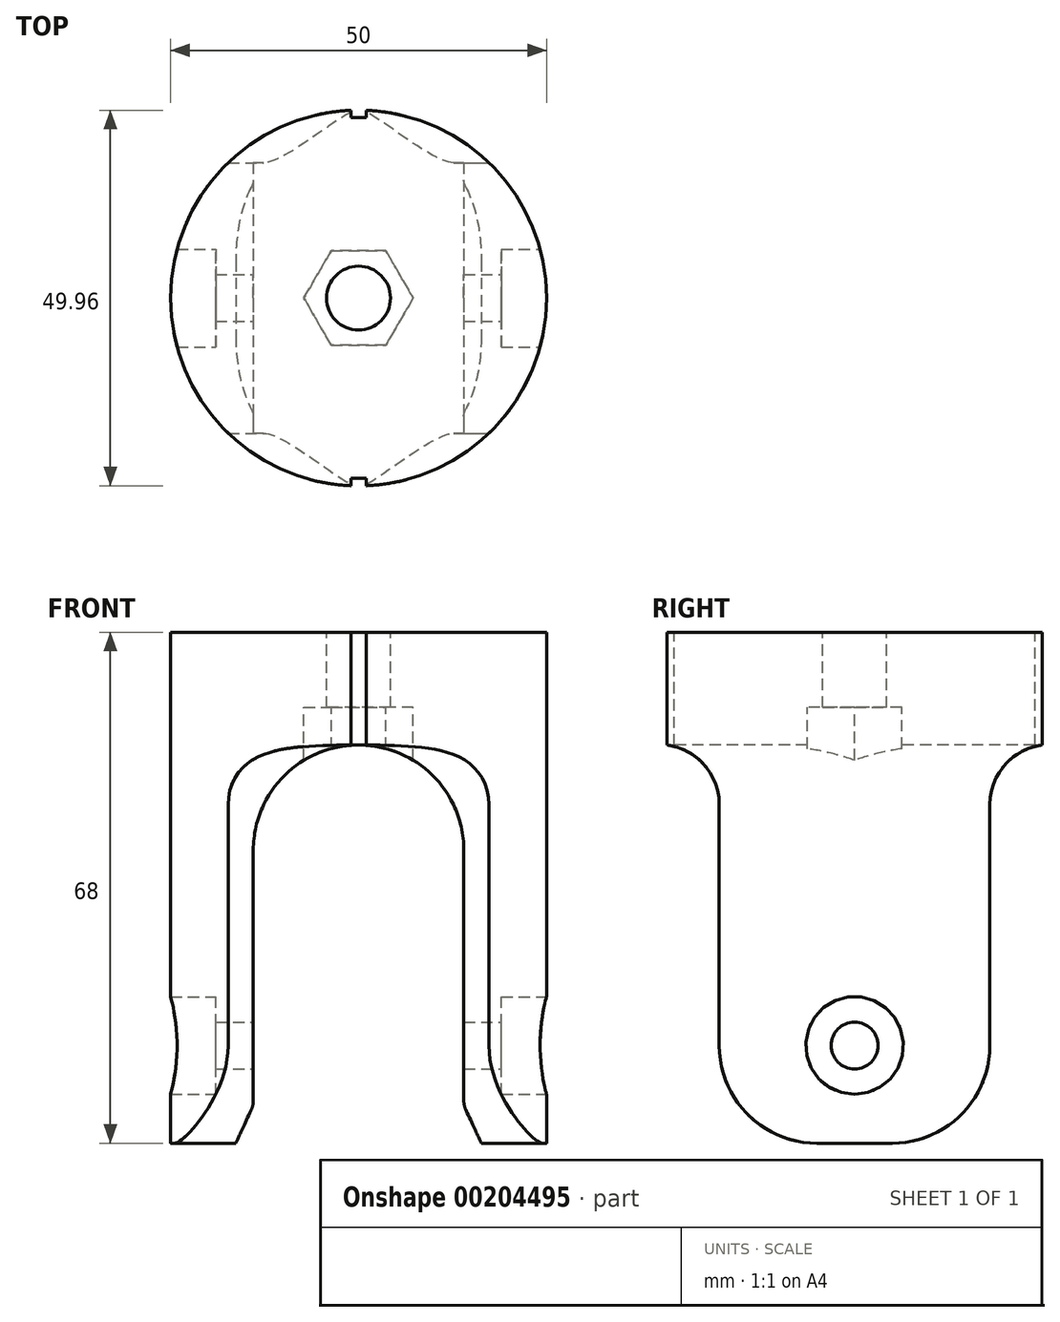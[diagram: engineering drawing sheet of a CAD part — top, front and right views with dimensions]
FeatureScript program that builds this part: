
annotation { "Feature Type Name" : "Feature", "Feature Type Description" : "" }
export const myFeature = defineFeature(function(context is Context, id is Id, definition is map)
    precondition{}
    {
        {
            var Q0;
            Q0=qCreatedBy(makeId("Top.planeOp"),FACE);
            var sketch = newSketch(context, id + "F0", { "sketchPlane" : qUnion([Q0])});
            skCircle(sketch, "E0", {"center": v(0, 0) * mm, "radius": 25 * mm});
            skSolve(sketch);
        }
        {
            var Q0;
            Q0 = qSketchRegion(id + "F0", true);
            extrude(context, id + "F1", {"entities" : qUnion([Q0]), "oppositeDirection" : true, "depth" : 68 * mm});
        }
        {
            var Q0;
            Q0=qCreatedBy(makeId("Right.planeOp"),FACE);
            var sketch = newSketch(context, id + "F2", { "sketchPlane" : qUnion([Q0])});
            skCircle(sketch, "E1", {"center": v(0, -55) * mm, "radius": 40 * mm, "construction": true});
            skLineSegment(sketch, "E2", {"start": v(-28, -15) * mm, "end": v(-25, -15) * mm});
            skLineSegment(sketch, "E3", {"start": v(-18, -22.94) * mm, "end": v(-18, -55) * mm});
            skLineSegment(sketch, "E4", {"start": v(-28, -15) * mm, "end": v(-28, -73) * mm});
            skLineSegment(sketch, "E5", {"start": v(-28, -73) * mm, "end": v(0, -73) * mm});
            skLineSegment(sketch, "E6", {"start": v(0, -68) * mm, "end": v(-5, -68) * mm});
            skArc(sketch, "E7", {"start": v(-18, -55) * mm, "mid": v(-14.2, -64.2) * mm, "end": v(-5, -68) * mm});
            skLineSegment(sketch, "E8", {"start": v(0, 0) * mm, "end": v(0, -95) * mm, "construction": true});
            skArc(sketch, "E9", {"start": v(-18, -22.94) * mm, "mid": v(-20, -17.65) * mm, "end": v(-25, -15) * mm});
            skLineSegment(sketch, "E10.MirrorCS", {"start": v(28, -15) * mm, "end": v(25, -15) * mm});
            skArc(sketch, "E11.MirrorCS", {"start": v(18, -22.94) * mm, "mid": v(20, -17.65) * mm, "end": v(25, -15) * mm});
            skArc(sketch, "E12.MirrorCS", {"start": v(18, -55) * mm, "mid": v(14.2, -64.2) * mm, "end": v(5, -68) * mm});
            skLineSegment(sketch, "E13.MirrorCS", {"start": v(0, -68) * mm, "end": v(5, -68) * mm});
            skLineSegment(sketch, "E14.MirrorCS", {"start": v(18, -22.94) * mm, "end": v(18, -55) * mm});
            skLineSegment(sketch, "E15.MirrorCS", {"start": v(28, -73) * mm, "end": v(0, -73) * mm});
            skLineSegment(sketch, "E16.MirrorCS", {"start": v(28, -15) * mm, "end": v(28, -73) * mm});
            skSolve(sketch);
        }
        {
            var Q0;
            Q0 = qSketchRegion(id + "F2", true);
            extrude(context, id + "F3", {"entities" : qUnion([Q0]), "operationType" : NewBodyOperationType.REMOVE, "endBound" : BoundingType.THROUGH_ALL, "oppositeDirection" : true, "depth" : 25 * mm, "hasSecondDirection" : true, "secondDirectionBound" : SecondDirectionBoundingType.THROUGH_ALL, "secondDirectionOppositeDirection" : false, "secondDirectionDepth" : 25 * mm});
        }
        {
            var Q0;
            Q0=qCreatedBy(makeId("Front.planeOp"),FACE);
            var sketch = newSketch(context, id + "F4", { "sketchPlane" : qUnion([Q0])});
            skArc(sketch, "E17", {"start": v(14, -29) * mm, "mid": v(0, -15) * mm, "end": v(-14, -29) * mm});
            skLineSegment(sketch, "E18", {"start": v(-14, -29) * mm, "end": v(-14, -62.33) * mm});
            skLineSegment(sketch, "E19", {"start": v(14, -29) * mm, "end": v(14, -62.33) * mm});
            skLineSegment(sketch, "E20", {"start": v(16.33, -68) * mm, "end": v(-16.33, -68) * mm});
            skLineSegment(sketch, "E21", {"start": v(-14.28, -63.6) * mm, "end": v(-16.33, -68) * mm});
            skLineSegment(sketch, "E22", {"start": v(14.28, -63.6) * mm, "end": v(16.33, -68) * mm});
            skLineSegment(sketch, "E23", {"start": v(-14, -63) * mm, "end": v(14, -63) * mm, "construction": true});
            skPoint(sketch, "E24.visualSharp", {"position": v(-14, -63) * mm});
            skArc(sketch, "E24.filletArc", {"start": v(-14.28, -63.6) * mm, "mid": v(-14.07, -62.98) * mm, "end": v(-14, -62.33) * mm});
            skPoint(sketch, "E25.visualSharp", {"position": v(14, -63) * mm});
            skArc(sketch, "E25.filletArc", {"start": v(14, -62.33) * mm, "mid": v(14.07, -62.98) * mm, "end": v(14.28, -63.6) * mm});
            skSolve(sketch);
        }
        {
            var Q0;
            Q0 = qSketchRegion(id + "F4", true);
            extrude(context, id + "F5", {"entities" : qUnion([Q0]), "operationType" : NewBodyOperationType.REMOVE, "endBound" : BoundingType.THROUGH_ALL, "oppositeDirection" : true, "depth" : 25 * mm, "hasSecondDirection" : true, "secondDirectionBound" : SecondDirectionBoundingType.THROUGH_ALL, "secondDirectionOppositeDirection" : false, "secondDirectionDepth" : 25 * mm});
        }
        {
            var Q0;
            Q0=qCreatedBy(makeId("Front.planeOp"),FACE);
            var sketch = newSketch(context, id + "F6", { "sketchPlane" : qUnion([Q0])});
            skLineSegment(sketch, "E26", {"start": v(-30.91, -55) * mm, "end": v(31.05, -55) * mm, "construction": true});
            skLineSegment(sketch, "E27", {"start": v(-26, -48.5) * mm, "end": v(-19, -48.5) * mm});
            skLineSegment(sketch, "E28", {"start": v(-19, -48.5) * mm, "end": v(-19, -51.88) * mm});
            skLineSegment(sketch, "E29", {"start": v(-19, -51.88) * mm, "end": v(0, -51.88) * mm});
            skLineSegment(sketch, "E30", {"start": v(-26, -48.5) * mm, "end": v(-26, -55) * mm});
            skLineSegment(sketch, "E31", {"start": v(-26, -55) * mm, "end": v(0, -55) * mm});
            skLineSegment(sketch, "E32.MirrorCS", {"start": v(26, -48.5) * mm, "end": v(19, -48.5) * mm});
            skLineSegment(sketch, "E33.MirrorCS", {"start": v(19, -48.5) * mm, "end": v(19, -51.88) * mm});
            skLineSegment(sketch, "E34.MirrorCS", {"start": v(19, -51.88) * mm, "end": v(0, -51.88) * mm});
            skLineSegment(sketch, "E35.MirrorCS", {"start": v(26, -48.5) * mm, "end": v(26, -55) * mm});
            skLineSegment(sketch, "E36.MirrorCS", {"start": v(26, -55) * mm, "end": v(0, -55) * mm});
            skSolve(sketch);
        }
        {
            var Q0;
            Q0 = qSketchRegion(id + "F6", true);
            var Q1;
            Q1=sQuery(id+"F6.wireOp",EDGE,"E26");
            revolve(context, id + "F7", {"operationType" : NewBodyOperationType.REMOVE, "entities" : qUnion([Q0]), "axis" : qUnion([Q1]), "revolveType" : RevolveType.FULL, "oppositeDirection" : true});
        }
        {
            var Q0;
            Q0=makeQuery(id+"F1.opExtrude","CAP_FACE",FACE,{"disambiguationData":[OSD([sQuery(id+"F0.wireOp",EDGE,"E0")])],"isStart":true});
            var sketch = newSketch(context, id + "F8", { "sketchPlane" : qUnion([Q0])});
            skCircle(sketch, "E37", {"center": v(0, 0) * mm, "radius": 4.25 * mm});
            skSolve(sketch);
        }
        {
            var Q0;
            Q0 = qSketchRegion(id + "F8", true);
            extrude(context, id + "F9", {"entities" : qUnion([Q0]), "operationType" : NewBodyOperationType.REMOVE, "oppositeDirection" : true, "depth" : 25 * mm});
        }
        {
            var Q0;
            Q0=qCreatedBy(makeId("Top.planeOp"),FACE);
            cPlane(context, id + "F10", {"entities" : qUnion([Q0]), "cplaneType" : CPlaneType.OFFSET, "offset" : 10 * mm, "oppositeDirection" : true, "width" : 150 * mm, "height" : 150 * mm});
        }
        {
            var Q0;
            Q0=qCreatedBy(id+"F10.planeOp",FACE);
            var sketch = newSketch(context, id + "F11", { "sketchPlane" : qUnion([Q0])});
            skCircle(sketch, "E38.cCircle", {"center": v(0, 0) * mm, "radius": 6.3 * mm, "construction": true});
            skLineSegment(sketch, "E38.0", {"start": v(7.27, 0) * mm, "end": v(3.64, -6.3) * mm});
            skLineSegment(sketch, "E38.1", {"start": v(3.64, -6.3) * mm, "end": v(-3.64, -6.3) * mm});
            skLineSegment(sketch, "E38.2", {"start": v(-3.64, -6.3) * mm, "end": v(-7.27, 0) * mm});
            skLineSegment(sketch, "E38.3", {"start": v(-7.27, 0) * mm, "end": v(-3.64, 6.3) * mm});
            skLineSegment(sketch, "E38.4", {"start": v(-3.64, 6.3) * mm, "end": v(3.64, 6.3) * mm});
            skLineSegment(sketch, "E38.5", {"start": v(3.64, 6.3) * mm, "end": v(7.27, 0) * mm});
            skPoint(sketch, "E38.0.midPoint", {"position": v(5.46, -3.15) * mm});
            skSolve(sketch);
        }
        {
            var Q0;
            Q0 = qSketchRegion(id + "F11", true);
            extrude(context, id + "F12", {"entities" : qUnion([Q0]), "operationType" : NewBodyOperationType.REMOVE, "oppositeDirection" : true, "depth" : 10 * mm});
        }
        {
            var Q0;
            Q0=makeQuery(id+"F1.opExtrude","CAP_FACE",FACE,{"disambiguationData":[OSD([sQuery(id+"F0.wireOp",EDGE,"E0")])],"isStart":true});
            var sketch = newSketch(context, id + "F13", { "sketchPlane" : qUnion([Q0])});
            skLineSegment(sketch, "E39.bottom", {"start": v(-1, 24) * mm, "end": v(1, 24) * mm});
            skLineSegment(sketch, "E39.top", {"start": v(-1, 26) * mm, "end": v(1, 26) * mm});
            skLineSegment(sketch, "E39.left", {"start": v(-1, 24) * mm, "end": v(-1, 26) * mm});
            skLineSegment(sketch, "E39.right", {"start": v(1, 24) * mm, "end": v(1, 26) * mm});
            skLineSegment(sketch, "E40.bottom", {"start": v(-1, -26) * mm, "end": v(1, -26) * mm});
            skLineSegment(sketch, "E40.top", {"start": v(-1, -24) * mm, "end": v(1, -24) * mm});
            skLineSegment(sketch, "E40.left", {"start": v(-1, -26) * mm, "end": v(-1, -24) * mm});
            skLineSegment(sketch, "E40.right", {"start": v(1, -26) * mm, "end": v(1, -24) * mm});
            skLineSegment(sketch, "E41", {"start": v(0, 18.47) * mm, "end": v(0, -17.11) * mm, "construction": true});
            skPoint(sketch, "E42", {"position": v(0, 24) * mm});
            skPoint(sketch, "E43", {"position": v(0, -24) * mm});
            skSolve(sketch);
        }
        {
            var Q0;
            Q0 = qSketchRegion(id + "F13", true);
            extrude(context, id + "F14", {"entities" : qUnion([Q0]), "operationType" : NewBodyOperationType.REMOVE, "oppositeDirection" : true, "depth" : 25 * mm});
        }
    });
